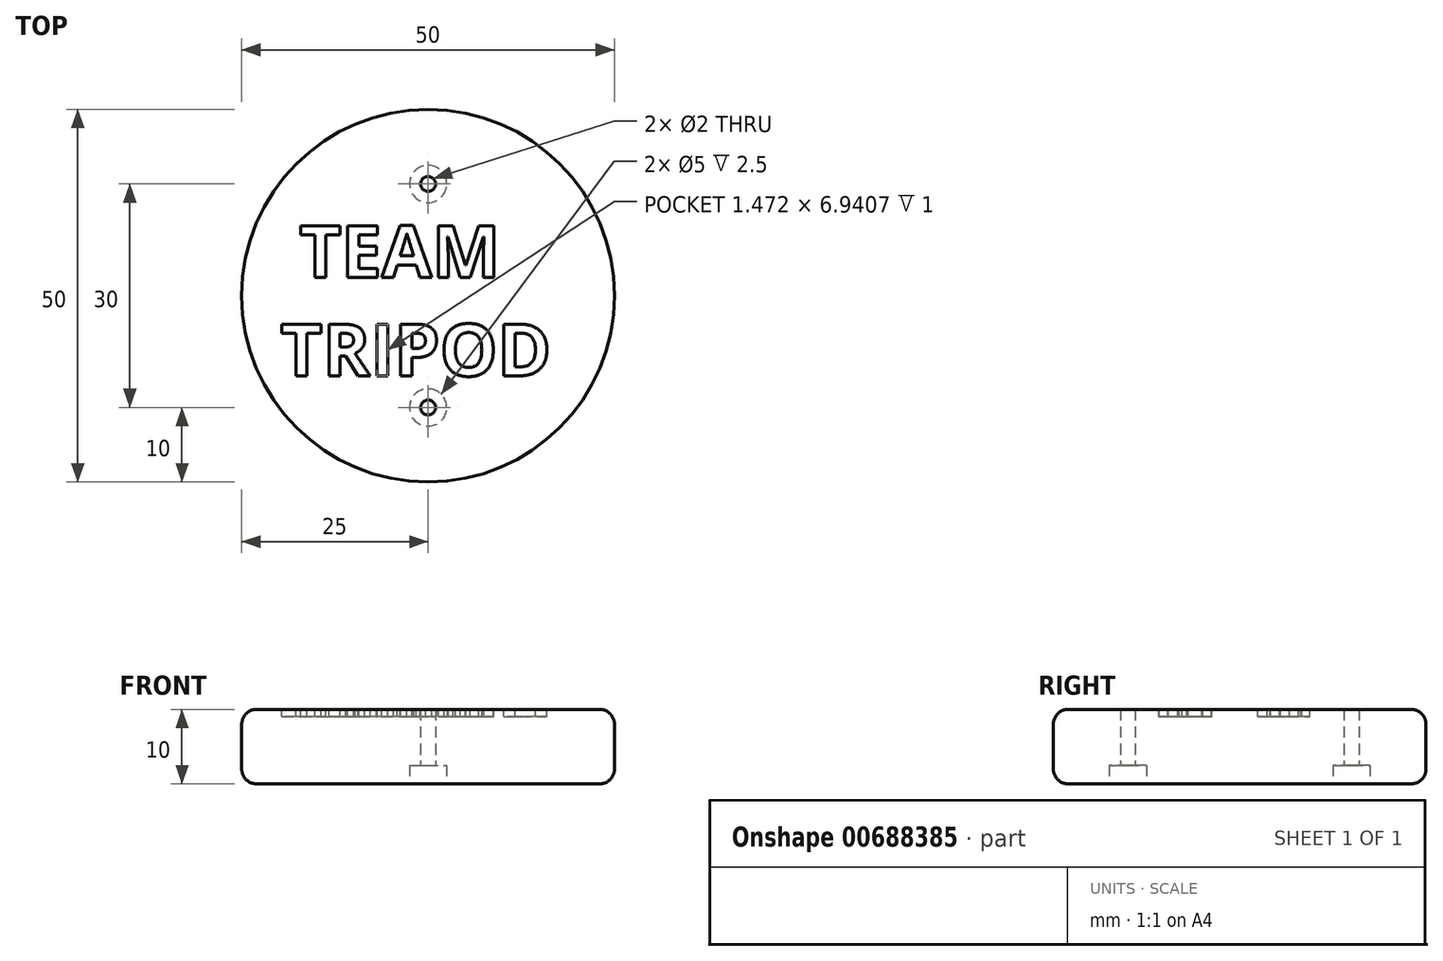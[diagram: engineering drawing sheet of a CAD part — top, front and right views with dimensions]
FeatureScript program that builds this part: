
annotation { "Feature Type Name" : "Feature", "Feature Type Description" : "" }
export const myFeature = defineFeature(function(context is Context, id is Id, definition is map)
    precondition{}
    {
        {
            var Q0;
            Q0=qCreatedBy(makeId("Top.planeOp"),FACE);
            var sketch = newSketch(context, id + "F0", { "sketchPlane" : qUnion([Q0])});
            skCircle(sketch, "E0", {"center": v(0, 0) * mm, "radius": 25 * mm});
            skSolve(sketch);
        }
        {
            var Q0;
            Q0=qSketchRegion(id+"F0",true);
            extrude(context, id + "F1", {"entities" : qUnion([Q0]), "depth" : 10 * mm});
        }
        {
            var Q0;
            Q0=makeQuery(id+"F1.opExtrude","CAP_FACE",FACE,{"disambiguationData":[OSD([sQuery(id+"F0.wireOp",EDGE,"E0")])],"isStart":false});
            var sketch = newSketch(context, id + "F2", { "sketchPlane" : qUnion([Q0])});
            skText(sketch, "E1", { "text": " TEAM \nTRIPOD", "fontName": "OpenSans-Bold.ttf"});
            const initialGuessF2  = {"E1": [-0.0198, 0.00246, 1, 0, 0.007]};
            skSetInitialGuess(sketch, initialGuessF2);
            skSolve(sketch);
        }
        {
            var Q0;
            Q0=qSketchRegion(id+"F2",true);
            extrude(context, id + "F3", {"entities" : qUnion([Q0]), "operationType" : NewBodyOperationType.REMOVE, "oppositeDirection" : true, "depth" : 1 * mm});
        }
        {
            var Q0;
            Q0=makeQuery(id+"F1.opExtrude","CAP_EDGE",EDGE,{"disambiguationData":[OSD([sQuery(id+"F0.wireOp",EDGE,"E0")])],"isStart":false});
            var Q1;
            Q1=makeQuery(id+"F1.opExtrude","CAP_EDGE",EDGE,{"disambiguationData":[OSD([sQuery(id+"F0.wireOp",EDGE,"E0")])],"isStart":true});
            fillet(context, id + "F4", {"entities" : qUnion([Q0, Q1]), "radius" : 2 * mm, "tangentPropagation" : true, "allowEdgeOverflow" : false});
        }
        {
            var Q0;
            Q0=makeQuery(id+"F1.opExtrude","CAP_FACE",FACE,{"disambiguationData":[OSD([sQuery(id+"F0.wireOp",EDGE,"E0")])],"isStart":true});
            var sketch = newSketch(context, id + "F5", { "sketchPlane" : qUnion([Q0])});
            skPoint(sketch, "E2", {"position": v(0, 15) * mm});
            skPoint(sketch, "E3", {"position": v(0, -15) * mm});
            skSolve(sketch);
        }
        {
            var Q0;
            Q0=sQuery(id+"F5.wireOp",VERTEX,"E2");
            var Q1;
            Q1=sQuery(id+"F5.wireOp",VERTEX,"E3");
            var Q2;
            Q2=makeQuery(id+"F1.opExtrude","SWEPT_BODY",BODY,{"disambiguationData":[OSD([sQuery(id+"F0.wireOp",EDGE,"E0")])]});
            hole(context, id + "F6", {"style" : HoleStyle.C_BORE, "endStyle" : HoleEndStyle.THROUGH, "holeDiameter" : 2 * mm, "cBoreDiameter" : 5 * mm, "cBoreDepth" : 2.5 * mm, "startFromSketch" : true, "locations" : qUnion([Q0, Q1]), "scope" : qUnion([Q2]), "isTappedThrough" : true});
        }
    });
